# Revit family: K8.2 - Yoke Mount
name_source: partatom
category: Generic Models
revit_build: Autodesk Revit 2017 (Build: 20190508_0315(x64)
units: mm (PartAtom-declared; Revit-internal decimal feet)

## family parameters
Can host rebar = No
Cut with Voids When Loaded = No
Host = Face
Part Type = Normal
Room Calculation Point = No
Round Connector Dimension = Use Diameter
Shared = No

## types (4) — shared parameters
Coverage Horizontal = 105.00°
Coverage Vertical = 105.00°
Depth = 269 mm  [stored 0.882546 ft]
Description = Multi-purpose, 2-way active loudspeaker
Height = 449 mm  [stored 1.4731 ft]
Manufacturer = QSC, LLC
Manufacturer URL = www.qsc.com
Model = K8.2
Mount Depth = 401 mm
Mount Width = 115 mm
Product Documentation Link = https://www.qsc.com
Product Page URL = https://www.qsc.com
Regulatory Compliance = CE, RAEE, UL, China RoHS, RoHS II, FCC Class B
SPL Max = 128
Weight Dimensional (kg) = 14.4
Weight Dimensional (lb) = 31.8
Weight Product (kg) = 12.2
Weight Product (lb) = 27
Width = 280 mm  [stored 0.918635 ft]
zero-valued in all types: Default Elevation

## per-type parameters (varying)
| type | End Pivot Speaker Distance From Mount | Outer Yoke Width | Show End Pivot Model | Show Side Pivot Model | Side Pivot Speaker Distance From Mount |
| Side-Pivot, Furthest Position | 265 mm  [stored 0.869423 ft] | 314 mm  [stored 1.03018 ft] | No | Yes | 266 mm  [stored 0.872703 ft] |
| Side-Pivot, Nearest Position | 265 mm  [stored 0.869423 ft] | 314 mm  [stored 1.03018 ft] | No | Yes | 202 mm  [stored 0.66273 ft] |
| End-Pivot, Furthest Position | 265 mm  [stored 0.869423 ft] | 499 mm  [stored 1.63714 ft] | Yes | No | 266 mm  [stored 0.872703 ft] |
| End-Pivot, Nearest Position | 201 mm  [stored 0.659449 ft] | 499 mm  [stored 1.63714 ft] | Yes | No | 266 mm  [stored 0.872703 ft] |

note: [stored X ft] marks values corroborated as IEEE doubles in the binary element streams (Revit-internal decimal feet)

## geometry (parser evidence)
native form markers: Blend x4, Sweep x13
no freeform markers — native parametric forms only
